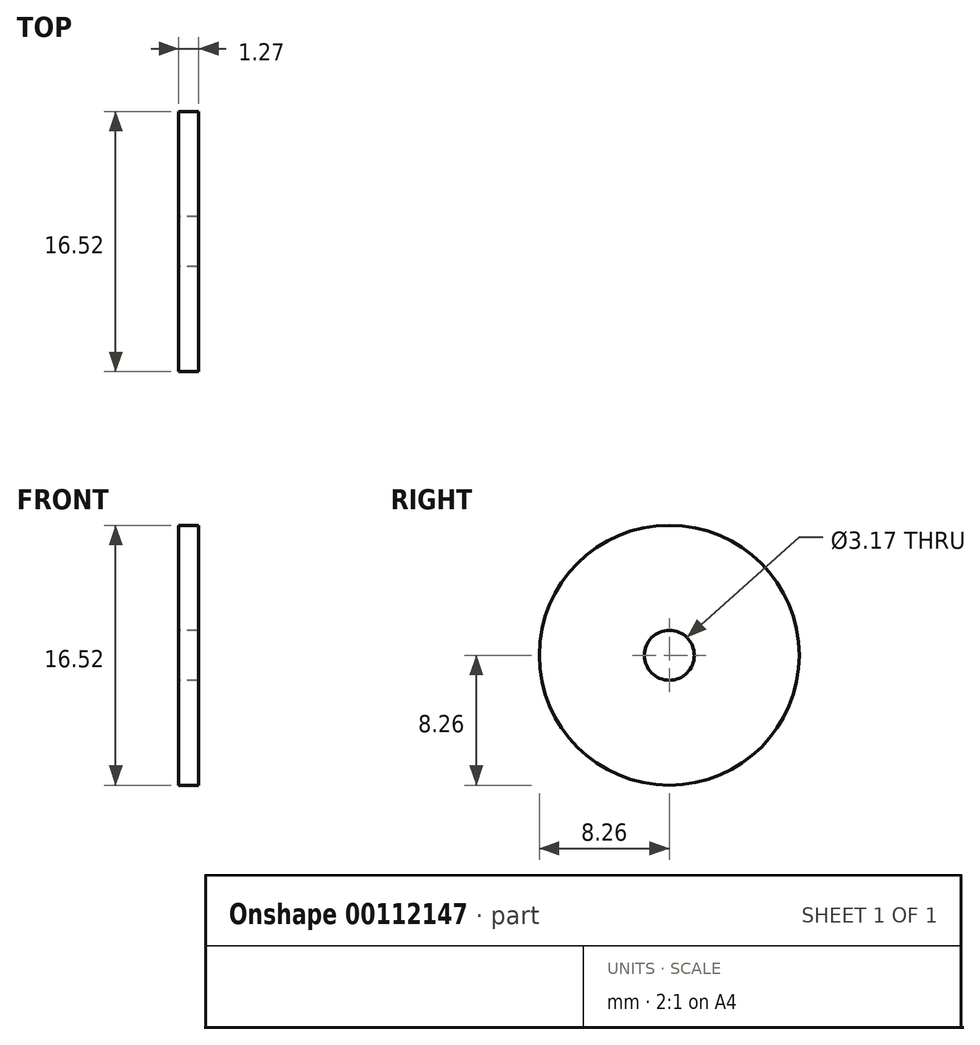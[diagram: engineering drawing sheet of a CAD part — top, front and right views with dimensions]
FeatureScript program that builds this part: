
annotation { "Feature Type Name" : "Feature", "Feature Type Description" : "" }
export const myFeature = defineFeature(function(context is Context, id is Id, definition is map)
    precondition{}
    {
        {
            var Q0;
            Q0=qCreatedBy(makeId("Right.planeOp"),FACE);
            var sketch = newSketch(context, id + "F0", { "sketchPlane" : qUnion([Q0])});
            skCircle(sketch, "E0", {"center": v(0, 0) * mm, "radius": 8.26 * mm});
            skCircle(sketch, "E1", {"center": v(0, 0) * mm, "radius": 1.59 * mm});
            skSolve(sketch);
        }
        {
            var Q0;
            Q0 = qSketchRegion(id + "F0", true);
            extrude(context, id + "F1", {"entities" : qUnion([Q0]), "depth" : 1.27 * mm});
        }
    });
